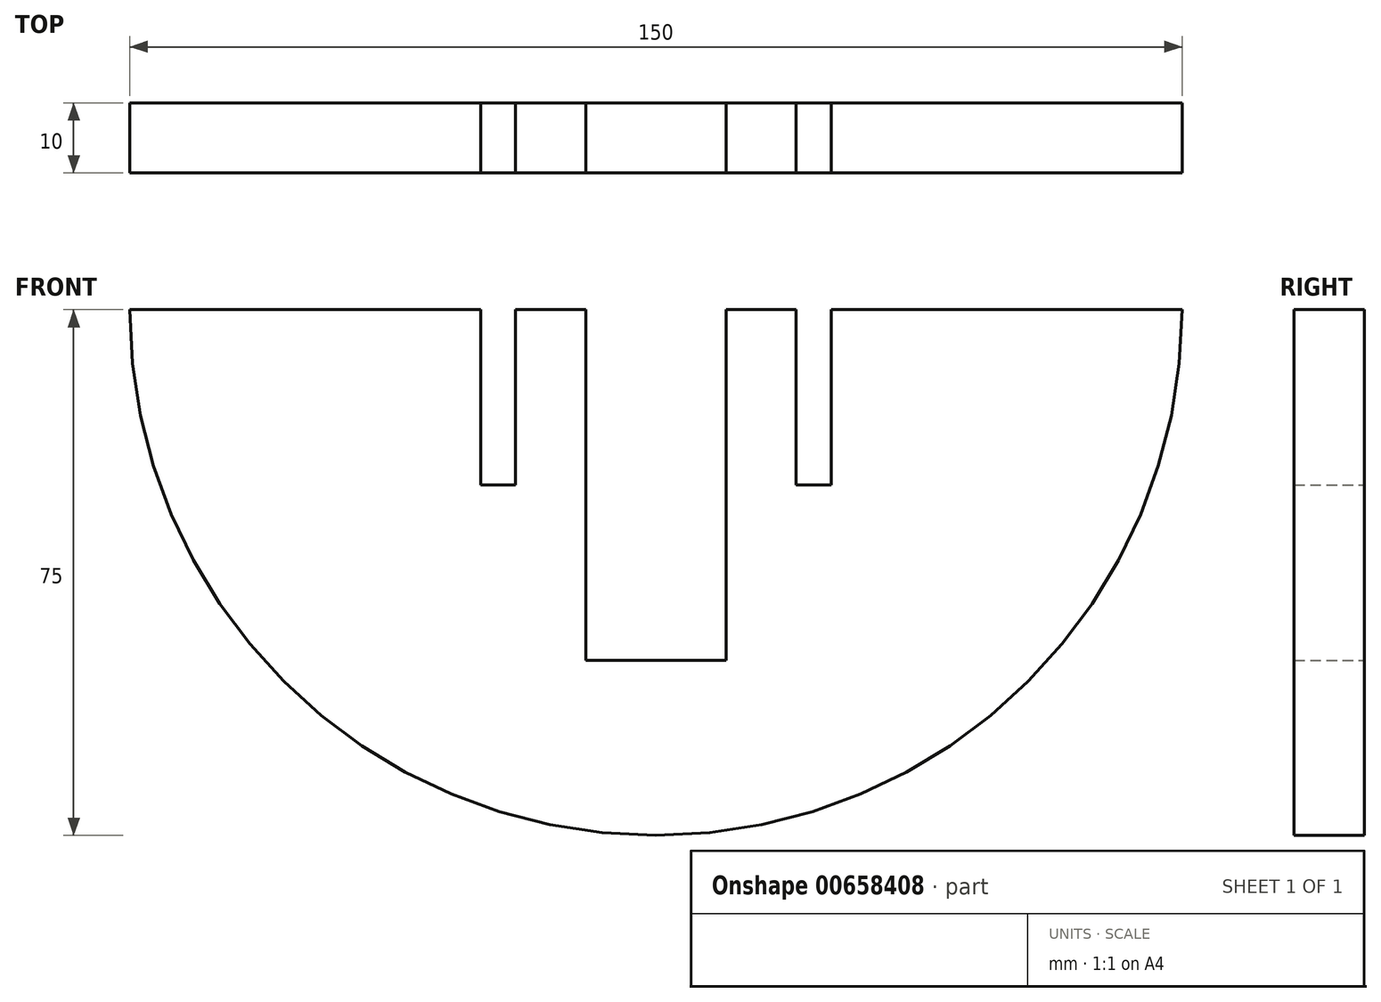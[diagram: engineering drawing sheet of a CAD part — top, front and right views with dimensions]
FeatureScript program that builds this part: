
annotation { "Feature Type Name" : "Feature", "Feature Type Description" : "" }
export const myFeature = defineFeature(function(context is Context, id is Id, definition is map)
    precondition{}
    {
        {
            var Q0;
            Q0=qCreatedBy(makeId("Front.planeOp"),FACE);
            var sketch = newSketch(context, id + "F0", { "sketchPlane" : qUnion([Q0])});
            skLineSegment(sketch, "E0", {"start": v(-20, 18.56) * mm, "end": v(-20, -6.44) * mm});
            skLineSegment(sketch, "E1", {"start": v(-20, -6.44) * mm, "end": v(-25, -6.44) * mm});
            skLineSegment(sketch, "E2", {"start": v(-25, -6.44) * mm, "end": v(-25, 18.56) * mm});
            skLineSegment(sketch, "E3", {"start": v(-25, 18.56) * mm, "end": v(-75, 18.56) * mm});
            skArc(sketch, "E4", {"start": v(-75, 18.56) * mm, "mid": v(-53.03, -34.47) * mm, "end": v(0, -56.44) * mm});
            skLineSegment(sketch, "E5", {"start": v(0, 30.43) * mm, "end": v(0, -72.23) * mm, "construction": true});
            skLineSegment(sketch, "E6", {"start": v(-20, 18.56) * mm, "end": v(-10, 18.56) * mm});
            skLineSegment(sketch, "E7", {"start": v(-10, 18.56) * mm, "end": v(-10, -31.44) * mm});
            skLineSegment(sketch, "E8", {"start": v(-10, -31.44) * mm, "end": v(0, -31.44) * mm});
            skLineSegment(sketch, "E9.MirrorCS", {"start": v(10, 18.56) * mm, "end": v(10, -31.44) * mm});
            skLineSegment(sketch, "E10.MirrorCS", {"start": v(20, 18.56) * mm, "end": v(20, -6.44) * mm});
            skLineSegment(sketch, "E11.MirrorCS", {"start": v(10, -31.44) * mm, "end": v(0, -31.44) * mm});
            skArc(sketch, "E12.MirrorCS", {"start": v(75, 18.56) * mm, "mid": v(53.03, -34.47) * mm, "end": v(0, -56.44) * mm});
            skLineSegment(sketch, "E13.MirrorCS", {"start": v(25, 18.56) * mm, "end": v(75, 18.56) * mm});
            skLineSegment(sketch, "E14.MirrorCS", {"start": v(25, -6.44) * mm, "end": v(25, 18.56) * mm});
            skLineSegment(sketch, "E15.MirrorCS", {"start": v(20, -6.44) * mm, "end": v(25, -6.44) * mm});
            skLineSegment(sketch, "E16.MirrorCS", {"start": v(20, 18.56) * mm, "end": v(10, 18.56) * mm});
            skSolve(sketch);
        }
        {
            var Q0;
            Q0 = qSketchRegion(id + "F0", true);
            extrude(context, id + "F1", {"entities" : qUnion([Q0]), "depth" : 10 * mm, "offsetDistance" : 25 * mm});
        }
    });
